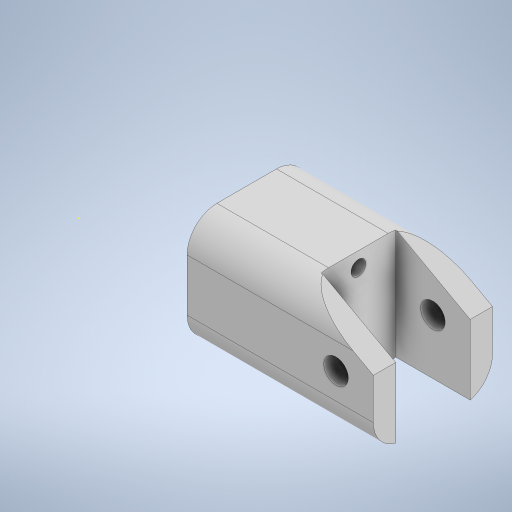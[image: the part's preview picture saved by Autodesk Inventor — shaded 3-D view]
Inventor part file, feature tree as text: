
AUTODESK INVENTOR PART (.ipt)
format: ipt  version: 2024 (Build 280153000, 153)  size: 482,816 bytes
history: native  units: mm
features: sketch x22, extrude x19, chamfer x3, plane x2, split x2, move_body x2, delete_face x1, fillet x1, boolean_combine x1
ambient origin geometry x8: Origin, YZ Plane, XZ Plane, XY Plane, X Axis, Y Axis, Z Axis, Center Point
bodies: Solid1 (feature_tree), Solid2 (feature_tree), Solid3 (feature_tree), Solid4 (feature_tree), Solid5 (feature_tree)
feature tree (53):
  extrude  "Extrusion1"  Depth=16.0mm
  sketch  "Sketch2"  dims[d2=15.0mm d3=0.0mm d4=10.0mm]
  extrude  "Extrusion2"  Depth=10.0mm
  chamfer  "Chamfer1"  Distance=21.25mm
  extrude  "Extrusion3"  Depth=10.0mm TaperAngle=0.0deg
  extrude  "Extrusion4"  Depth=11.5mm TaperAngle=0.0deg
  extrude  "Extrusion5"  Depth=1.0mm TaperAngle=0.0deg
  chamfer  "Chamfer2"  Distance=6.0mm Angle=45.0deg
  sketch  "Sketch6"  dims[d14=7.0mm d15=11.5mm d16=0.0mm]
  extrude  "Extrusion6"  Depth=15.0mm
  extrude  "Extrusion7"  Depth=5.5mm TaperAngle=0.0deg
  chamfer  "Chamfer3"  Distance=5.5mm Angle=45.0deg
  sketch  "Sketch9"  dims[d26=3.3mm d27=45.25mm d28=0.0mm d29=11.5mm d30=5.5mm d31=45.0deg]
  extrude  "Extrusion8"  Depth=65.75mm TaperAngle=0.0deg
  extrude  "Extrusion9"  Depth=0.5mm TaperAngle=0.0deg
  extrude  "Extrusion10"  Depth=13.0mm TaperAngle=0.0deg
  sketch  "Sketch13"  dims[d43=24.0mm d44=21.0mm d45=0.0mm]
  extrude  "Extrusion11"  Depth=21.0mm TaperAngle=0.0deg
  extrude  "Extrusion12"  TaperAngle=0.0deg  [1 undecoded]
  extrude  "Extrusion13"  Depth=4.0mm
  plane  "Work Plane1"
  split  "Split1"
  move_body  "Move Body1"
  extrude  "Extrusion14"  Depth=1.0mm
  delete_face  "Delete Face1"
  fillet  "Fillet1"  Radius=1.5mm
  extrude  "Extrusion17"  Depth=1.0mm
  extrude  "Extrusion18"  Depth=5.5mm TaperAngle=0.0deg
  extrude  "Extrusion19"  [1 undecoded]
  extrude  "Extrusion20"  Depth=3.0mm TaperAngle=0.0deg
  plane  "Work Plane2"
  split  "Split2"
  move_body  "Move Body2"
  extrude  "Extrusion21"  [1 undecoded]
  boolean_combine  "Combine1"
  sketch  "Sketch1"  dims[d0=36.0mm d1=16.0mm]
  sketch  "Sketch3"  dims[d5=10.0mm]
  sketch  "Sketch4"  dims[d6=3.3mm d7=21.25mm d8=0.0mm]
  sketch  "Sketch5"  dims[d9=10.0mm d10=5.5mm d11=45.0deg d12=10.0mm d13=0.0mm]
  sketch  "Sketch7"  dims[d17=3.3mm d18=1.0mm d19=0.0mm d20=6.0mm d21=11.5mm d22=45.0deg]
  sketch  "Sketch8"  dims[d23=15.0mm d24=0.0mm d25=9.0mm]
  sketch  "Sketch10"  dims[d32=2.0mm d33=65.75mm d34=0.0mm]
  sketch  "Sketch11"  dims[d35=0.5mm d36=0.0mm d37=9.0mm d38=0.0mm]
  sketch  "Sketch12"  dims[d39=0.5mm d40=0.0mm d41=13.0mm d42=0.0mm]
  sketch  "Sketch14"  dims[d46=12.25mm d47=-12.0mm d48=0.0mm d49=0.0mm]
  sketch  "Sketch15"  dims[d50=10.0mm d51=0.0mm d52=4.0mm]
  sketch  "Sketch16"  dims[d61=1.0mm d62=1.0mm d63=1.5mm d64=0.0mm]
  sketch  "Sketch17"  dims[d65=1.0mm d66=1.0mm]
  sketch  "Sketch20"  dims[d67=5.5mm d68=0.0mm d69=1.2mm d70=0.0mm]
  sketch  "Sketch21"  dims[d71=2.2mm d72=0.0mm d73=-5.5mm]
  sketch  "Sketch22"  dims[d74=-3.0mm d75=0.0mm d76=0.0mm d77=3.0mm d78=0.0mm]
  sketch  "Sketch23"  dims[d53=0.872665mm]
  sketch  "Sketch24"
note: 3 required parameter values undecoded (feature->parameter linkage not recoverable at this tier; creation-order binding heuristic only, values carry confidence <= 0.55)
